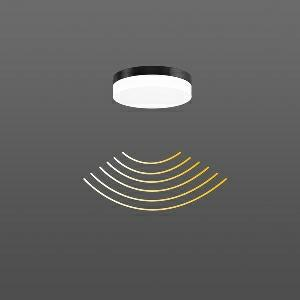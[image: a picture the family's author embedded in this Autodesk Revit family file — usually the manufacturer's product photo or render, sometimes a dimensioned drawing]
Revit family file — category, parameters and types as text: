
# Revit family: flat_slim_round_312135_0031_2_19_b40c
name_source: partatom
category: Lighting Fixtures
units: mm (PartAtom-declared; Revit-internal decimal feet)

## family parameters
Cut with Voids When Loaded = No
Host = Face
Light Source = No
Part Type = Normal
Room Calculation Point = No
Round Connector Dimension = Use Diameter
Shared = No

## types (1)
- FLAT SLIM round (1 x LED Modul 830, 1300 lm, 3000)
    Apparent Load = 12 VA
    CIE Flux Codes = 43 74 92 91 100
    Color Rendering = 80
    Color Temperature = 3000
    Default Elevation = 1800 mm
    Height = 63 mm
    Lamp = 1 x LED Modul 830
    Lamp Light Flux = 1300 lm
    Lamp count = 1
    Length = 230 mm
    Lifetime = 50000 h
    Luminous efficacy = 108 lm/W
    Manufacturer = RZB
    ModVariant = No
    Model = 312135.0031.2.19
    Mounting Place = Ceiling, Wall
    Mounting Type = Surface mounted
    Number of Poles = 1
    OnlyDefault = Yes
    Power Factor = 1
    Product Name = FLAT SLIM round
    Product group = Surface mounted ceiling and wall luminaires
    ProductGroupID = 305
    Protection Class = Protection class I
    Protection Degree = IP 65
    RLX_Detail_Level = 1
    RLX_Emergency_Light_Flux = 0 lm
    RLX_Emergency_Type = 0
    RLX_Emergency_Type_DB = No
    RlxData = <blob elided: 34633 chars, md5=76c637cb>
    Socket = socket
    Standby Power = 0 W
    System Light Flux = 1300 lm
    System Power = 12 W
    Type Comments = Product without accessories
    Type Image = 312132.0031.19.jpg
    URL = http://relux.com
    VarID = ---
    Voltage = 230 V
    Voltage Range = 220-240 V
    Weight = 0.00 kg
    Width = 0 mm  [stored 0 ft]

note: [stored X ft] marks values corroborated as IEEE doubles in the binary element streams (Revit-internal decimal feet)

## geometry (parser evidence)
native form markers: Blend x4, Sweep x12
no freeform markers — native parametric forms only
